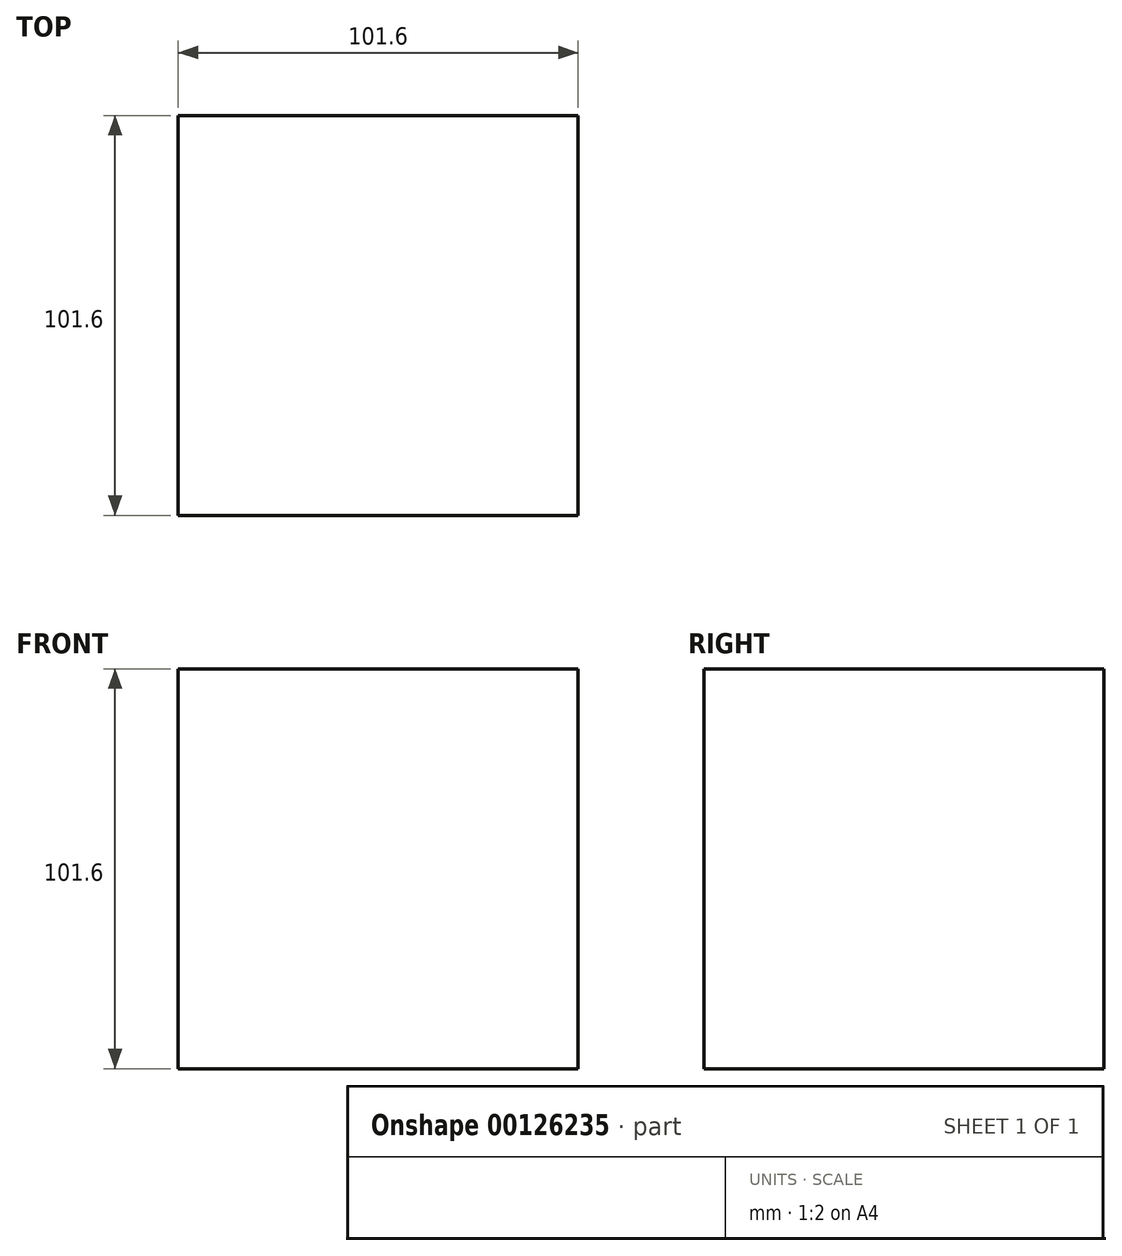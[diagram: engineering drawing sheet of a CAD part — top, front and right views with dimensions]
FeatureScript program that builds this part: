
annotation { "Feature Type Name" : "Feature", "Feature Type Description" : "" }
export const myFeature = defineFeature(function(context is Context, id is Id, definition is map)
    precondition{}
    {
        {
            var Q0;
            Q0=qCreatedBy(makeId("Front.planeOp"),FACE);
            var sketch = newSketch(context, id + "F0", { "sketchPlane" : qUnion([Q0])});
            skLineSegment(sketch, "E0.bottom", {"start": v(50.8, 50.8) * mm, "end": v(-50.8, 50.8) * mm});
            skLineSegment(sketch, "E0.top", {"start": v(50.8, -50.8) * mm, "end": v(-50.8, -50.8) * mm});
            skLineSegment(sketch, "E0.left", {"start": v(50.8, 50.8) * mm, "end": v(50.8, -50.8) * mm});
            skLineSegment(sketch, "E0.right", {"start": v(-50.8, 50.8) * mm, "end": v(-50.8, -50.8) * mm});
            skPoint(sketch, "E0.middle", {"position": v(0, 0) * mm});
            skSolve(sketch);
        }
        {
            var Q0;
            Q0 = qSketchRegion(id + "F0", true);
            extrude(context, id + "F1", {"entities" : qUnion([Q0]), "depth" : 101.6 * mm});
        }
    });
